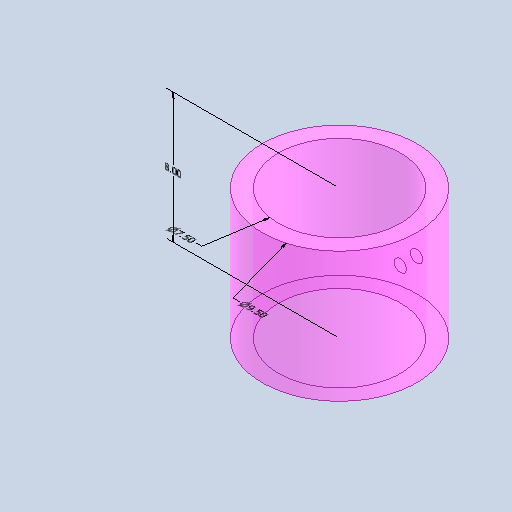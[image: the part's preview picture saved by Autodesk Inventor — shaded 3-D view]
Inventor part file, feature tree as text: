
AUTODESK INVENTOR PART (.ipt)
format: ipt  version: 2022 (Build 260153000, 153)  size: 138,752 bytes
history: native  units: in
note: dims shown in document units (in); Inventor stores cm internally (conversion verified against a paired STEP export)
features: other x4, extrude x2, sketch x2
ambient origin geometry x8: Origin, YZ Plane, XZ Plane, XY Plane, X Axis, Y Axis, Z Axis, Center Point
bodies: Solid1 (feature_tree)
feature tree (8):
  other  "Annotations"
  extrude  "Extrusion1"  Depth=1.0in
  extrude  "Extrusion2"  Depth=8.0in
  sketch  "Sketch1"  dims[d0=7.5in d1=1.0in]
  sketch  "Sketch2"  dims[d2=8.0in d3=0.0in d5=0.75in d6=2.0in d7=0.0in d8=0.0in d10=7.5in d11=0.7267in d12=9.5in d4=8.0in d9=0.5578in]
  other  "Linear Dimension 1"
  other  "Diameter Dimension 1"
  other  "Diameter Dimension 2"
